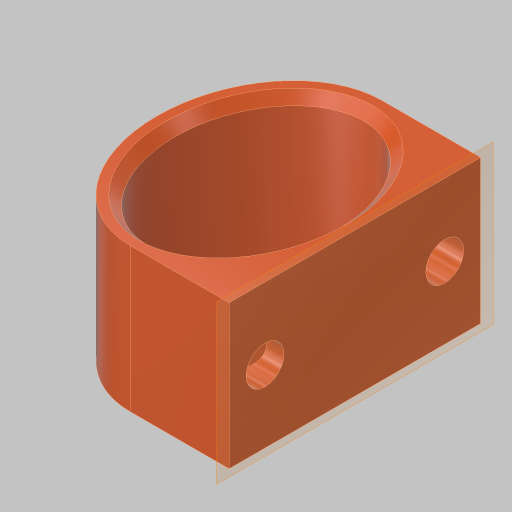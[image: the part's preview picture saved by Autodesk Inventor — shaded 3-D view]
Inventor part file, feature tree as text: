
AUTODESK INVENTOR PART (.ipt)
format: ipt  version: 2023.5 (Build 275446000, 446)  size: 172,544 bytes
history: native  units: in
note: dims shown in document units (in); Inventor stores cm internally (conversion verified against a paired STEP export)
features: extrude x2, sketch x2, chamfer x1, plane x1, projected_geometry x1
ambient origin geometry x8: Origin, YZ Plane, XZ Plane, XY Plane, X Axis, Y Axis, Z Axis, Center Point
bodies: Solid1 (feature_tree)
feature tree (7):
  extrude  "Extrusion1"  Depth=0.875in
  chamfer  "Chamfer1"  Distance=1.0in
  plane  "Work Plane1"
  extrude  "Extrusion2"  Depth=0.0625in TaperAngle=45.0deg
  sketch  "Sketch1"  dims[d0=0.6875in d1=0.875in]
  sketch  "Sketch2"  dims[d2=0.125in d3=1.0in d4=0.0in d5=0.0625in d6=0.125in d7=45.0deg d8=0.688in d9=1.25in d10=0.5in d11=0.2638in d12=1.0in d13=0.0in]
  projected_geometry  "Projected Loop1"
